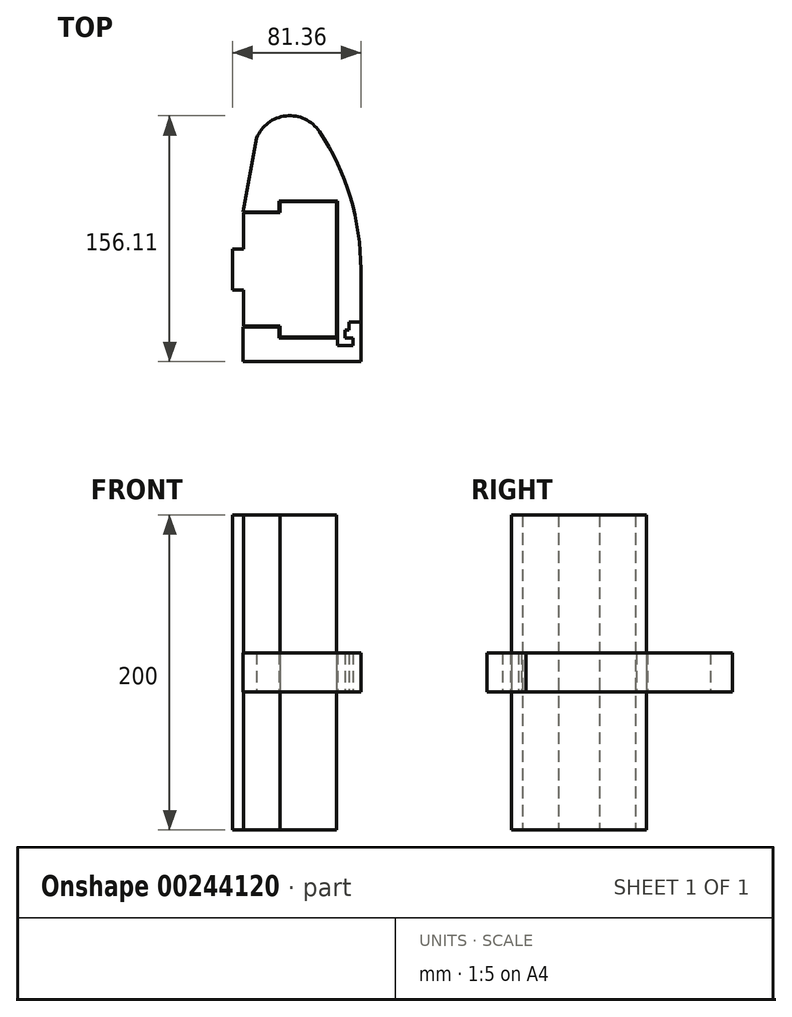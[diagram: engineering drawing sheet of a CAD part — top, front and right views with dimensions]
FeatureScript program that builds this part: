
annotation { "Feature Type Name" : "Feature", "Feature Type Description" : "" }
export const myFeature = defineFeature(function(context is Context, id is Id, definition is map)
    precondition{}
    {
        {
            var Q0;
            Q0=qCreatedBy(makeId("Top.planeOp"),FACE);
            var sketch = newSketch(context, id + "F0", { "sketchPlane" : qUnion([Q0])});
            skLineSegment(sketch, "E0.bottom", {"start": v(18, -43) * mm, "end": v(-18, -43) * mm});
            skLineSegment(sketch, "E0.top", {"start": v(18, 43) * mm, "end": v(-18, 43) * mm});
            skLineSegment(sketch, "E0.left", {"start": v(18, -43) * mm, "end": v(18, 43) * mm});
            skLineSegment(sketch, "E0.right", {"start": v(-18, -43) * mm, "end": v(-18, 43) * mm});
            skPoint(sketch, "E0.middle", {"position": v(0, 0) * mm});
            skLineSegment(sketch, "E1.bottom", {"start": v(-18, 36) * mm, "end": v(-41, 36) * mm});
            skLineSegment(sketch, "E1.top", {"start": v(-18, 13) * mm, "end": v(-41, 13) * mm});
            skLineSegment(sketch, "E1.left", {"start": v(-18, 36) * mm, "end": v(-18, 13) * mm});
            skLineSegment(sketch, "E1.right", {"start": v(-41, 36) * mm, "end": v(-41, 13) * mm});
            skLineSegment(sketch, "E2.bottom", {"start": v(-18, -36) * mm, "end": v(-41, -36) * mm});
            skLineSegment(sketch, "E2.top", {"start": v(-18, -13) * mm, "end": v(-41, -13) * mm});
            skLineSegment(sketch, "E2.left", {"start": v(-18, -36) * mm, "end": v(-18, -13) * mm});
            skLineSegment(sketch, "E2.right", {"start": v(-41, -36) * mm, "end": v(-41, -13) * mm});
            skLineSegment(sketch, "E3.bottom", {"start": v(-47.86, -13) * mm, "end": v(-18, -13) * mm});
            skLineSegment(sketch, "E3.top", {"start": v(-47.86, 13) * mm, "end": v(-18, 13) * mm});
            skLineSegment(sketch, "E3.left", {"start": v(-47.86, -13) * mm, "end": v(-47.86, 13) * mm});
            skLineSegment(sketch, "E3.right", {"start": v(-18, -13) * mm, "end": v(-18, 13) * mm});
            skLineSegment(sketch, "E4", {"start": v(18, 0) * mm, "end": v(-47.86, 0) * mm, "construction": true});
            skSolve(sketch);
        }
        {
            var Q0;
            {var subQ1=sQuery(id+"F0.wireOp",EDGE,"E0.bottom");Q0=makeQuery(id+"F0.imprint","IMPRINT",FACE,{"disambiguationData":[TD([[makeQuery(id+"F0.imprint","IMPRINT",EDGE,{"derivedFrom":subQ1}),-1.0]])]});}
            var Q1;
            Q1=makeQuery(id+"F0.imprint","IMPRINT",FACE,{"disambiguationData":[TD([[makeQuery(id+"F0.imprint","IMPRINT",EDGE,{"derivedFrom":sQuery(id+"F0.wireOp",EDGE,"E2.bottom")}),-1.0]])]});
            var Q2;
            Q2=makeQuery(id+"F0.imprint","IMPRINT",FACE,{"disambiguationData":[TD([[makeQuery(id+"F0.imprint","IMPRINT",EDGE,{"derivedFrom":sQuery(id+"F0.wireOp",EDGE,"E1.bottom")}),1.0]])]});
            var Q3;
            {var subQ3=sQuery(id+"F0.wireOp",EDGE,"E3.left");Q3=makeQuery(id+"F0.imprint","IMPRINT",FACE,{"disambiguationData":[TD([[makeQuery(id+"F0.imprint","IMPRINT",EDGE,{"derivedFrom":subQ3}),-1.0]])]});}
            extrude(context, id + "F1", {"entities" : qUnion([Q0, Q1, Q2, Q3]), "depth" : 200 * mm, "offsetDistance" : 25 * mm, "symmetric" : true});
        }
        {
            var Q0;
            Q0=qCreatedBy(makeId("Top.planeOp"),FACE);
            var sketch = newSketch(context, id + "F2", { "sketchPlane" : qUnion([Q0])});
            skLineSegment(sketch, "E5.0", {"start": v(-18, -36) * mm, "end": v(-41, -36) * mm, "construction": true});
            skLineSegment(sketch, "E6.0", {"start": v(-18, -43) * mm, "end": v(-18, -36) * mm, "construction": true});
            skLineSegment(sketch, "E7.0", {"start": v(18, -43) * mm, "end": v(-18, -43) * mm, "construction": true});
            skLineSegment(sketch, "E8.0", {"start": v(18, -43) * mm, "end": v(18, 43) * mm, "construction": true});
            skLineSegment(sketch, "E9.0", {"start": v(18, 43) * mm, "end": v(-18, 43) * mm, "construction": true});
            skLineSegment(sketch, "E10.0", {"start": v(-18, 36) * mm, "end": v(-18, 43) * mm, "construction": true});
            skLineSegment(sketch, "E11.0", {"start": v(-18, 36) * mm, "end": v(-41, 36) * mm, "construction": true});
            skLineSegment(sketch, "E12.0", {"start": v(-18.5, 36.5) * mm, "end": v(-41.37, 36.5) * mm});
            skLineSegment(sketch, "E12.1", {"start": v(-18.5, 36.5) * mm, "end": v(-18.5, 43.5) * mm});
            skLineSegment(sketch, "E12.2", {"start": v(18.5, 43.5) * mm, "end": v(-18.5, 43.5) * mm});
            skLineSegment(sketch, "E12.3", {"start": v(-18.5, -36.5) * mm, "end": v(-41.37, -36.5) * mm});
            skLineSegment(sketch, "E12.4", {"start": v(-18.5, -43.5) * mm, "end": v(-18.5, -36.5) * mm});
            skLineSegment(sketch, "E12.5", {"start": v(18.5, -43.5) * mm, "end": v(-18.5, -43.5) * mm});
            skLineSegment(sketch, "E12.6", {"start": v(18.5, -48.5) * mm, "end": v(18.5, 43.5) * mm});
            skPoint(sketch, "E13", {"position": v(-125, 0) * mm});
            skLineSegment(sketch, "E14", {"start": v(-41.37, -36.5) * mm, "end": v(-41.37, -58.5) * mm});
            skLineSegment(sketch, "E15", {"start": v(-41.37, -58.5) * mm, "end": v(33.5, -58.5) * mm});
            skLineSegment(sketch, "E16", {"start": v(33.5, -58.5) * mm, "end": v(33.5, -33.5) * mm});
            skLineSegment(sketch, "E17", {"start": v(-32.7, 83.37) * mm, "end": v(-41.37, 36.5) * mm});
            skArc(sketch, "E18", {"start": v(33.5, 0) * mm, "mid": v(26.78, 45.68) * mm, "end": v(7.17, 87.48) * mm});
            skArc(sketch, "E19", {"start": v(7.17, 87.48) * mm, "mid": v(-14, 97.5) * mm, "end": v(-32.7, 83.37) * mm});
            skLineSegment(sketch, "E20", {"start": v(23.5, -43.5) * mm, "end": v(23.5, -38.5) * mm});
            skLineSegment(sketch, "E21", {"start": v(23.5, -38.5) * mm, "end": v(26, -38.5) * mm});
            skLineSegment(sketch, "E22", {"start": v(18.5, -48.5) * mm, "end": v(28.5, -48.5) * mm});
            skLineSegment(sketch, "E23", {"start": v(33.5, -38.5) * mm, "end": v(33.5, -38.5) * mm});
            skLineSegment(sketch, "E24", {"start": v(33.5, -33.5) * mm, "end": v(33.5, 0) * mm});
            skLineSegment(sketch, "E25", {"start": v(28.5, -48.5) * mm, "end": v(28.5, -43.5) * mm});
            skLineSegment(sketch, "E26", {"start": v(28.5, -43.5) * mm, "end": v(23.5, -43.5) * mm});
            skLineSegment(sketch, "E27", {"start": v(33.5, -33.5) * mm, "end": v(26, -33.5) * mm});
            skLineSegment(sketch, "E28", {"start": v(26, -33.5) * mm, "end": v(26, -38.5) * mm});
            skPoint(sketch, "E29", {"position": v(0, 0) * mm});
            skSolve(sketch);
        }
        {
            var Q0;
            Q0=makeQuery(id+"F2.imprint","IMPRINT",FACE,{"disambiguationData":[TD([[makeQuery(id+"F2.imprint","IMPRINT",EDGE,{"derivedFrom":sQuery(id+"F2.wireOp",EDGE,"E12.3")}),1.0]])]});
            extrude(context, id + "F3", {"entities" : qUnion([Q0]), "depth" : 25 * mm, "offsetDistance" : 25 * mm, "symmetric" : true});
        }
        {
            var Q0;
            Q0=makeQuery(id+"F2.imprint","IMPRINT",FACE,{"disambiguationData":[TD([[makeQuery(id+"F2.imprint","IMPRINT",EDGE,{"derivedFrom":sQuery(id+"F2.wireOp",EDGE,"E12.0")}),-1.0]])]});
            extrude(context, id + "F4", {"entities" : qUnion([Q0]), "depth" : 25 * mm, "offsetDistance" : 25 * mm, "symmetric" : true});
        }
    });
